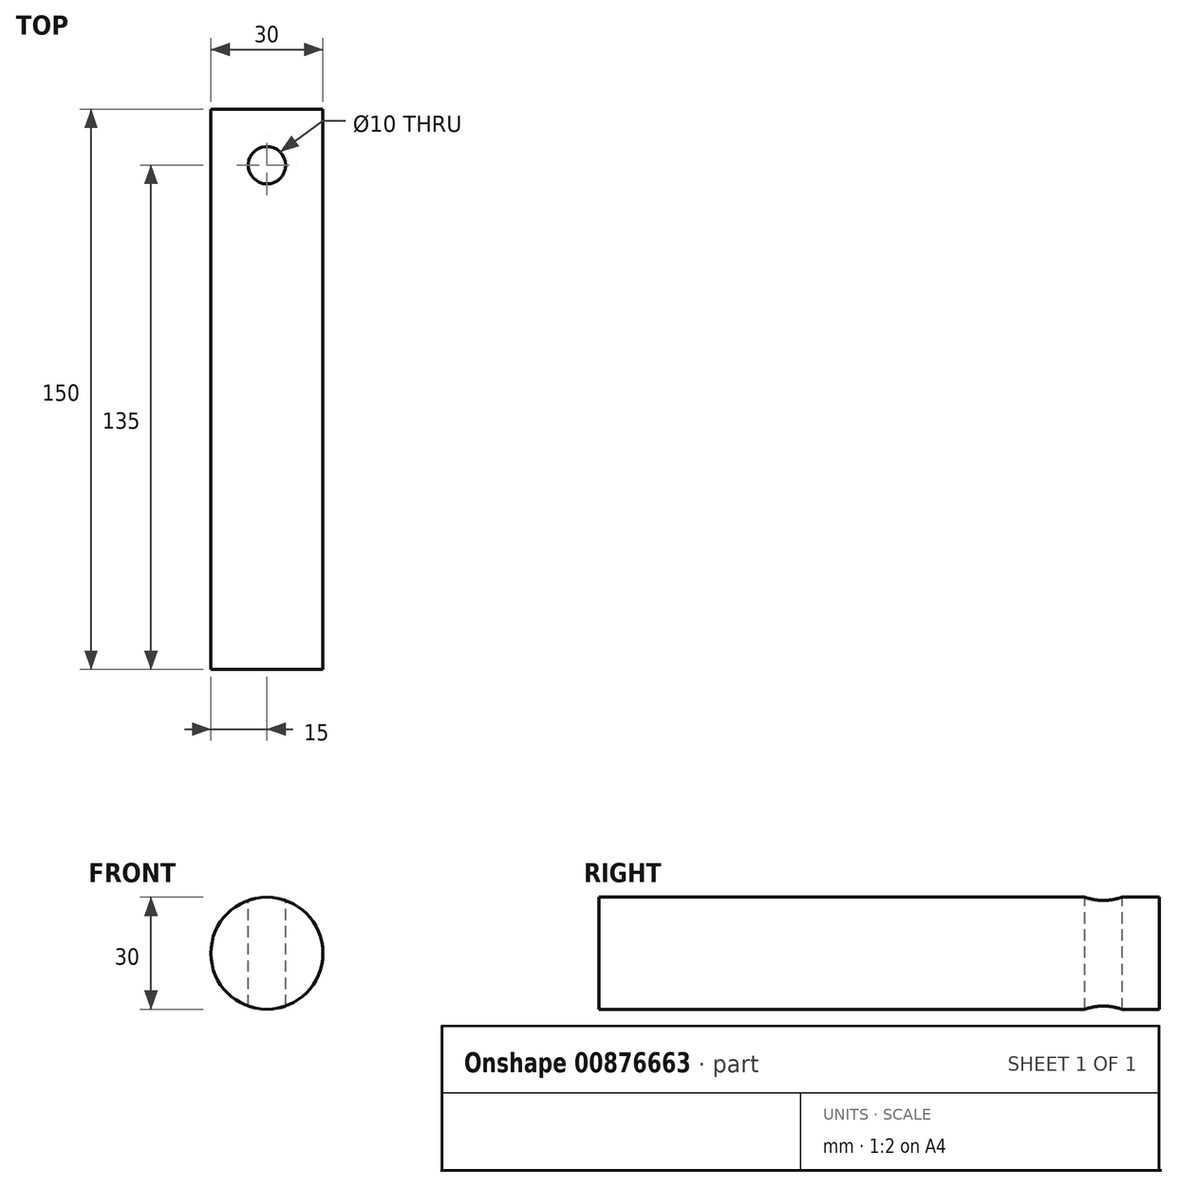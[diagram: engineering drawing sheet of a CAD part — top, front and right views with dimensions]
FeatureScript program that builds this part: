
annotation { "Feature Type Name" : "Feature", "Feature Type Description" : "" }
export const myFeature = defineFeature(function(context is Context, id is Id, definition is map)
    precondition{}
    {
        {
            var Q0;
            Q0=qCreatedBy(makeId("Front.planeOp"),FACE);
            var sketch = newSketch(context, id + "F0", { "sketchPlane" : qUnion([Q0])});
            skCircle(sketch, "E0", {"center": v(0, 0) * mm, "radius": 15 * mm});
            skSolve(sketch);
        }
        {
            var Q0;
            Q0=makeQuery(id+"F0.imprint","IMPRINT",FACE,{"disambiguationData":[TD([[makeQuery(id+"F0.imprint","IMPRINT",EDGE,{"derivedFrom":sQuery(id+"F0.wireOp",EDGE,"E0")}),-1.0]])]});
            var Q1;
            Q1=makeQuery(id+"F0.imprint","IMPRINT",FACE,{"disambiguationData":[TD([[makeQuery(id+"F0.imprint","IMPRINT",EDGE,{"derivedFrom":sQuery(id+"F0.wireOp",EDGE,"E0")}),1.0]])]});
            extrude(context, id + "F1", {"entities" : qUnion([Q0, Q1]), "depth" : 150 * mm, "offsetDistance" : 25 * mm});
        }
        {
            var Q0;
            Q0=qCreatedBy(makeId("Top.planeOp"),FACE);
            var sketch = newSketch(context, id + "F2", { "sketchPlane" : qUnion([Q0])});
            skCircle(sketch, "E1", {"center": v(0, 0) * mm, "radius": 15 * mm});
            skCircle(sketch, "E2", {"center": v(0, -15) * mm, "radius": 5 * mm});
            skSolve(sketch);
        }
        {
            var Q0;
            {var subQ0=sQuery(id+"F2.wireOp",EDGE,"E2");var subQ1=sQuery(id+"F2.wireOp",EDGE,"E1");var subQ2=makeQuery(id+"F2.imprint","INTERSECT",VERTEX,{"disambiguationData":[OD(0.0)],"derivedFrom":[subQ1,subQ0]});Q0=makeQuery(id+"F2.imprint","IMPRINT",FACE,{"disambiguationData":[TD([[makeQuery(id+"F2.imprint","IMPRINT",EDGE,{"disambiguationData":[TD([[subQ2,-1.0]])],"derivedFrom":subQ1}),-1.0]])]});}
            var Q1;
            {var subQ0=sQuery(id+"F2.wireOp",EDGE,"E2");var subQ1=sQuery(id+"F2.wireOp",EDGE,"E1");var subQ2=makeQuery(id+"F2.imprint","INTERSECT",VERTEX,{"disambiguationData":[OD(0.0)],"derivedFrom":[subQ1,subQ0]});Q1=makeQuery(id+"F2.imprint","IMPRINT",FACE,{"disambiguationData":[TD([[makeQuery(id+"F2.imprint","IMPRINT",EDGE,{"disambiguationData":[TD([[subQ2,-1.0]])],"derivedFrom":subQ1}),1.0]])]});}
            extrude(context, id + "F3", {"entities" : qUnion([Q0, Q1]), "operationType" : NewBodyOperationType.REMOVE, "oppositeDirection" : true, "depth" : 39.8 * mm, "offsetDistance" : 25 * mm, "symmetric" : true});
        }
    });
